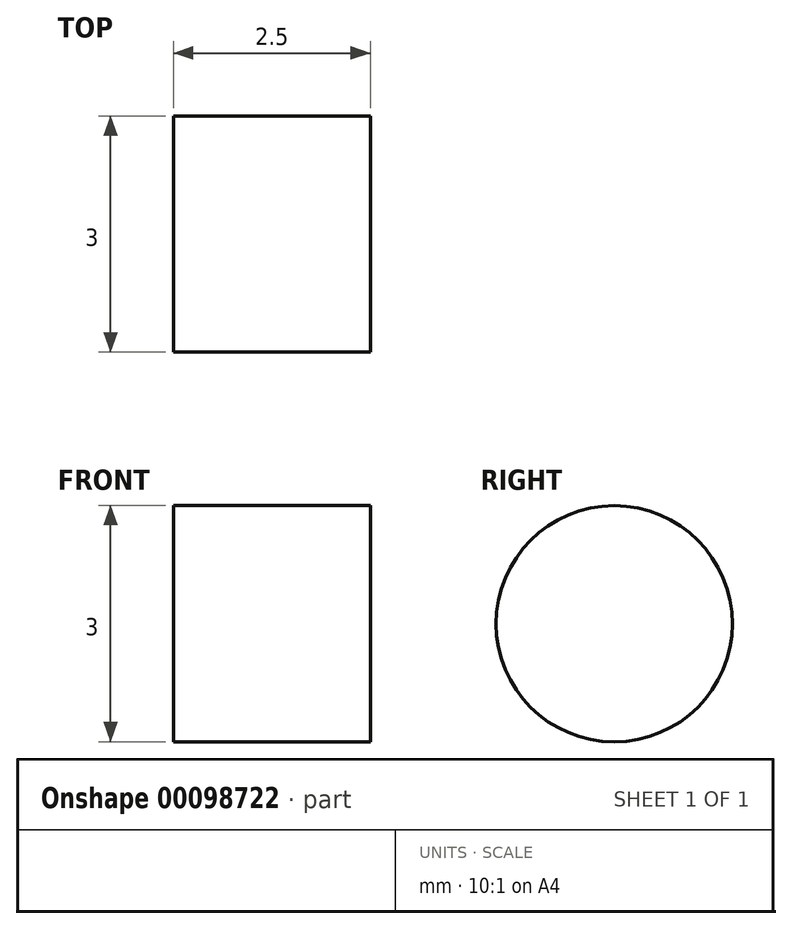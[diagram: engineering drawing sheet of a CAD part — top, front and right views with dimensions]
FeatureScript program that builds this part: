
annotation { "Feature Type Name" : "Feature", "Feature Type Description" : "" }
export const myFeature = defineFeature(function(context is Context, id is Id, definition is map)
    precondition{}
    {
        {
            var Q0;
            Q0=qCreatedBy(makeId("Right.planeOp"),FACE);
            var sketch = newSketch(context, id + "F0", { "sketchPlane" : qUnion([Q0])});
            skCircle(sketch, "E0", {"center": v(-39.76, 32.83) * mm, "radius": 1.5 * mm});
            skCircle(sketch, "E1", {"center": v(-39.76, -59.17) * mm, "radius": 1.5 * mm});
            skCircle(sketch, "E2", {"center": v(39.24, 66.83) * mm, "radius": 1.5 * mm});
            skCircle(sketch, "E3", {"center": v(-0.76, -64.17) * mm, "radius": 1.5 * mm});
            skCircle(sketch, "E4", {"center": v(4.74, 0.83) * mm, "radius": 6 * mm});
            skLineSegment(sketch, "E5", {"start": v(-14.19, -8.89) * mm, "end": v(5.8, 22.76) * mm});
            skArc(sketch, "E6", {"start": v(5.8, 22.76) * mm, "mid": v(5.86, 24.8) * mm, "end": v(4.1, 25.83) * mm});
            skLineSegment(sketch, "E7", {"start": v(4.1, 25.83) * mm, "end": v(-28.79, 25.83) * mm});
            skArc(sketch, "E8", {"start": v(-28.79, 25.83) * mm, "mid": v(-30.45, 24.94) * mm, "end": v(-30.64, 23.07) * mm});
            skLineSegment(sketch, "E9", {"start": v(-30.64, 23.07) * mm, "end": v(-17.73, -8.57) * mm});
            skArc(sketch, "E10", {"start": v(-17.73, -8.57) * mm, "mid": v(-16.05, -9.81) * mm, "end": v(-14.19, -8.89) * mm});
            skArc(sketch, "E11", {"start": v(-10.79, -59.53) * mm, "mid": v(-9.34, -58.55) * mm, "end": v(-9.2, -56.8) * mm});
            skLineSegment(sketch, "E12", {"start": v(-9.2, -56.8) * mm, "end": v(-16.81, -37.8) * mm});
            skArc(sketch, "E13", {"start": v(-16.81, -37.8) * mm, "mid": v(-18.48, -36.54) * mm, "end": v(-20.36, -37.46) * mm});
            skLineSegment(sketch, "E14", {"start": v(-20.36, -37.46) * mm, "end": v(-34.43, -59.51) * mm});
            skArc(sketch, "E15", {"start": v(-34.43, -59.51) * mm, "mid": v(-34.42, -61.67) * mm, "end": v(-32.46, -62.57) * mm});
            skLineSegment(sketch, "E16", {"start": v(-32.46, -62.57) * mm, "end": v(-10.79, -59.53) * mm});
            skLineSegment(sketch, "E17", {"start": v(-29.08, -32.97) * mm, "end": v(-23.32, -24.04) * mm});
            skArc(sketch, "E18", {"start": v(-23.32, -24.04) * mm, "mid": v(-23.01, -23.15) * mm, "end": v(-23.15, -22.21) * mm});
            skLineSegment(sketch, "E19", {"start": v(-23.15, -22.21) * mm, "end": v(-28.9, -7.81) * mm});
            skArc(sketch, "E20", {"start": v(-28.9, -7.81) * mm, "mid": v(-31.14, -6.6) * mm, "end": v(-32.76, -8.56) * mm});
            skLineSegment(sketch, "E21", {"start": v(-32.76, -8.56) * mm, "end": v(-32.76, -31.88) * mm});
            skArc(sketch, "E22", {"start": v(-32.76, -31.88) * mm, "mid": v(-31.33, -33.8) * mm, "end": v(-29.08, -32.97) * mm});
            skLineSegment(sketch, "E23", {"start": v(-11.26, -23.3) * mm, "end": v(-6.5, -15.1) * mm});
            skArc(sketch, "E24", {"start": v(-6.5, -15.1) * mm, "mid": v(-4.24, -14.17) * mm, "end": v(-2.76, -16.1) * mm});
            skLineSegment(sketch, "E25", {"start": v(-2.76, -16.1) * mm, "end": v(-2.76, -35.43) * mm});
            skArc(sketch, "E26", {"start": v(-2.76, -35.43) * mm, "mid": v(-4.36, -37.39) * mm, "end": v(-6.6, -36.22) * mm});
            skLineSegment(sketch, "E27", {"start": v(-6.6, -36.22) * mm, "end": v(-11.37, -25.1) * mm});
            skArc(sketch, "E28", {"start": v(-11.37, -25.1) * mm, "mid": v(-11.52, -24.19) * mm, "end": v(-11.26, -23.3) * mm});
            skLineSegment(sketch, "E29", {"start": v(-44.76, -56.67) * mm, "end": v(-44.76, -67.17) * mm});
            skArc(sketch, "E30", {"start": v(-44.76, -67.17) * mm, "mid": v(-43.3, -70.7) * mm, "end": v(-39.76, -72.17) * mm});
            skLineSegment(sketch, "E31", {"start": v(-39.76, -72.17) * mm, "end": v(-31.57, -72.17) * mm});
            skArc(sketch, "E32", {"start": v(-31.57, -72.17) * mm, "mid": v(-31.26, -72.16) * mm, "end": v(-30.95, -72.13) * mm});
            skLineSegment(sketch, "E33", {"start": v(-30.95, -72.13) * mm, "end": v(-7.57, -69.21) * mm});
            skArc(sketch, "E34", {"start": v(-7.57, -69.21) * mm, "mid": v(-7.26, -69.18) * mm, "end": v(-6.95, -69.17) * mm});
            skLineSegment(sketch, "E35", {"start": v(-6.95, -69.17) * mm, "end": v(-0.76, -69.17) * mm});
            skArc(sketch, "E36", {"start": v(-0.76, -69.17) * mm, "mid": v(2.77, -67.7) * mm, "end": v(4.24, -64.17) * mm});
            skLineSegment(sketch, "E37", {"start": v(4.24, -64.17) * mm, "end": v(4.24, -28.2) * mm});
            skArc(sketch, "E38", {"start": v(4.24, -28.2) * mm, "mid": v(4.34, -27.2) * mm, "end": v(4.64, -26.23) * mm});
            skLineSegment(sketch, "E39", {"start": v(4.64, -26.23) * mm, "end": v(44.35, 64.98) * mm});
            skArc(sketch, "E40", {"start": v(44.35, 64.98) * mm, "mid": v(44.46, 68.68) * mm, "end": v(42, 71.45) * mm});
            skLineSegment(sketch, "E41", {"start": v(42, 71.45) * mm, "end": v(41.6, 71.64) * mm});
            skArc(sketch, "E42", {"start": v(41.6, 71.64) * mm, "mid": v(37.84, 71.93) * mm, "end": v(34.95, 69.51) * mm});
            skLineSegment(sketch, "E43", {"start": v(34.95, 69.51) * mm, "end": v(23.12, 47.2) * mm});
            skArc(sketch, "E44", {"start": v(23.12, 47.2) * mm, "mid": v(18.7, 42.55) * mm, "end": v(12.52, 40.83) * mm});
            skLineSegment(sketch, "E45", {"start": v(12.52, 40.83) * mm, "end": v(-38.22, 40.83) * mm});
            skArc(sketch, "E46", {"start": v(-38.22, 40.83) * mm, "mid": v(-42.84, 38.71) * mm, "end": v(-44.26, 33.83) * mm});
            skArc(sketch, "E47", {"start": v(-44.26, 33.83) * mm, "mid": v(-41.06, -11.44) * mm, "end": v(-44.76, -56.67) * mm});
            skSolve(sketch);
        }
        {
            var Q0;
            Q0=makeQuery(id+"F0.imprint","IMPRINT",FACE,{"disambiguationData":[TD([[makeQuery(id+"F0.imprint","IMPRINT",EDGE,{"derivedFrom":sQuery(id+"F0.wireOp",EDGE,"E0")}),1.0]])]});
            extrude(context, id + "F1", {"entities" : qUnion([Q0]), "depth" : 2.5 * mm, "symmetric" : true});
        }
    });
